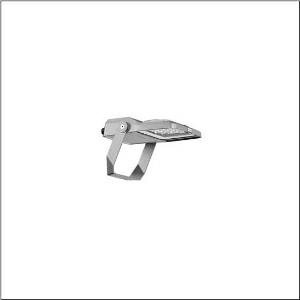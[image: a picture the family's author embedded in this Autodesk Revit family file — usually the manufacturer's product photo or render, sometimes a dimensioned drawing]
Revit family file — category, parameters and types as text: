
# Revit family: floodlight_fl_21_iq_micro___rs12_5xa7761a2b1a_22b8
name_source: partatom
category: Lighting Fixtures
units: mm (PartAtom-declared; Revit-internal decimal feet)

## family parameters
Cut with Voids When Loaded = No
Host = Face
Light Source = No
Part Type = Normal
Room Calculation Point = No
Round Connector Dimension = Use Diameter
Shared = No

## types (1)
- --- (1 x LED, 3090 lm, 23.1 W, 3000K)
    Apparent Load = 23 VA
    CIE Flux Codes = 79 92 99 100 100
    Color Rendering = 70
    Color Temperature = 3000K
    Default Elevation = 1800 mm
    Description = Floodlight FL 21 iQ micro, floodlight, primary light control with lens, of PMMA, primary optical cover: protective disc, of toughened safety glass, transparent, light distribution: RS12, light emission: direct distribution, installation type: surface-mounted, lamps: LED, High Power LED, rated values: 3.090lm | 23,1W | 133,8lm/W (begin service life); end service life: 3.090lm | 23,8W; at 50% lumin. flux: 1.545lm | 11W | 140,5lm/W, colour temperature: 3000K, colour rendering: CRI > 70, light colour: 730, light setting 1 begin service life: 100% | 3.090lm | 23,1W | 133,8lm/W | 3.000K, light setting 1 end service life: 23,8W, further light settings possible, control: optimised constant luminous flux control (CLO 2.0), Desk-Remote (wireless, voltage-free reading and setting of iQ features in the workshop via application-optimized NFC function/RFID function), Light-Fading, Smart-Wire, Night-Set, Lumen-Switch, Temp-Guard, Auto-Match, pre-setting: linear dimming characteristic, with terminal, 6-pole, mains connection: 220..240V, AC, 50/60Hz, luminaire housing, of diecast aluminium, powder-coated, SITECO metallic grey (DB 702S), corrosivity category C5 mid according to DIN EN ISO 12944suitable for swimming poolschlorine-resistant, sealing non-destructively replaceable, mounting bracket, of steel, galvanised, powder-coated, SITECO metallic grey (DB 702S), protection rating (complete): IP66, insulation class (complete): insulation class II (safety insulation), certification: CE, ENEC, VDE, protection symbol: D, impact resistance: IK07, permissible operating ambient temperature: -40..+40°C, permissible operating ambient temperature for outdoor applications: -40..+50°C, standard: DIN EN 12944, LABS conformity tested according to VDMA 24364:2018-05, packaging unit: 1 piece

Light Distribution: RS12
    Height = 65 mm
    Lamp = 1 x LED
    Lamp Light Flux = 3090 lm
    Lamp Power = 23.1 W
    Lamp count = 1
    Length = 312 mm
    Luminous efficacy = 134 lm/W
    Manufacturer = Siteco
    ModVariant = No
    Model = 5XA7761A2B1A
    Mounting Place = Wall
    Mounting Type = Surface mounted
    Number of Poles = 1
    OnlyDefault = Yes
    Power Factor = 1
    Product Name = Floodlight FL 21 iQ micro | RS12
    Product group = floodlight | wall mounted
    ProductGroupID = 2002
    Protection Class = Protection class II
    Protection Degree = IP 66
    RLX_Detail_Level = 1
    RLX_Emergency_Light_Flux = 0 lm
    RLX_Emergency_Type = 0
    RLX_Emergency_Type_DB = No
    RlxData = <blob elided: 75265 chars, md5=c3c9e43f>
    Socket = socket
    Standby Power = 0 W
    System Light Flux = 3090 lm
    System Power = 23 W
    Type Comments = factory setting: luminous flux: 100 % | dim-lin: 254 | 455 mA
    Type Image = l_1006880.jpg
    URL = http://relux.com
    VarID = @adj_179857
    Voltage = 0 V
    Weight = 0.00 kg
    Width = 230 mm

## geometry (parser evidence)
native form markers: Blend x4, Sweep x9
no freeform markers — native parametric forms only
